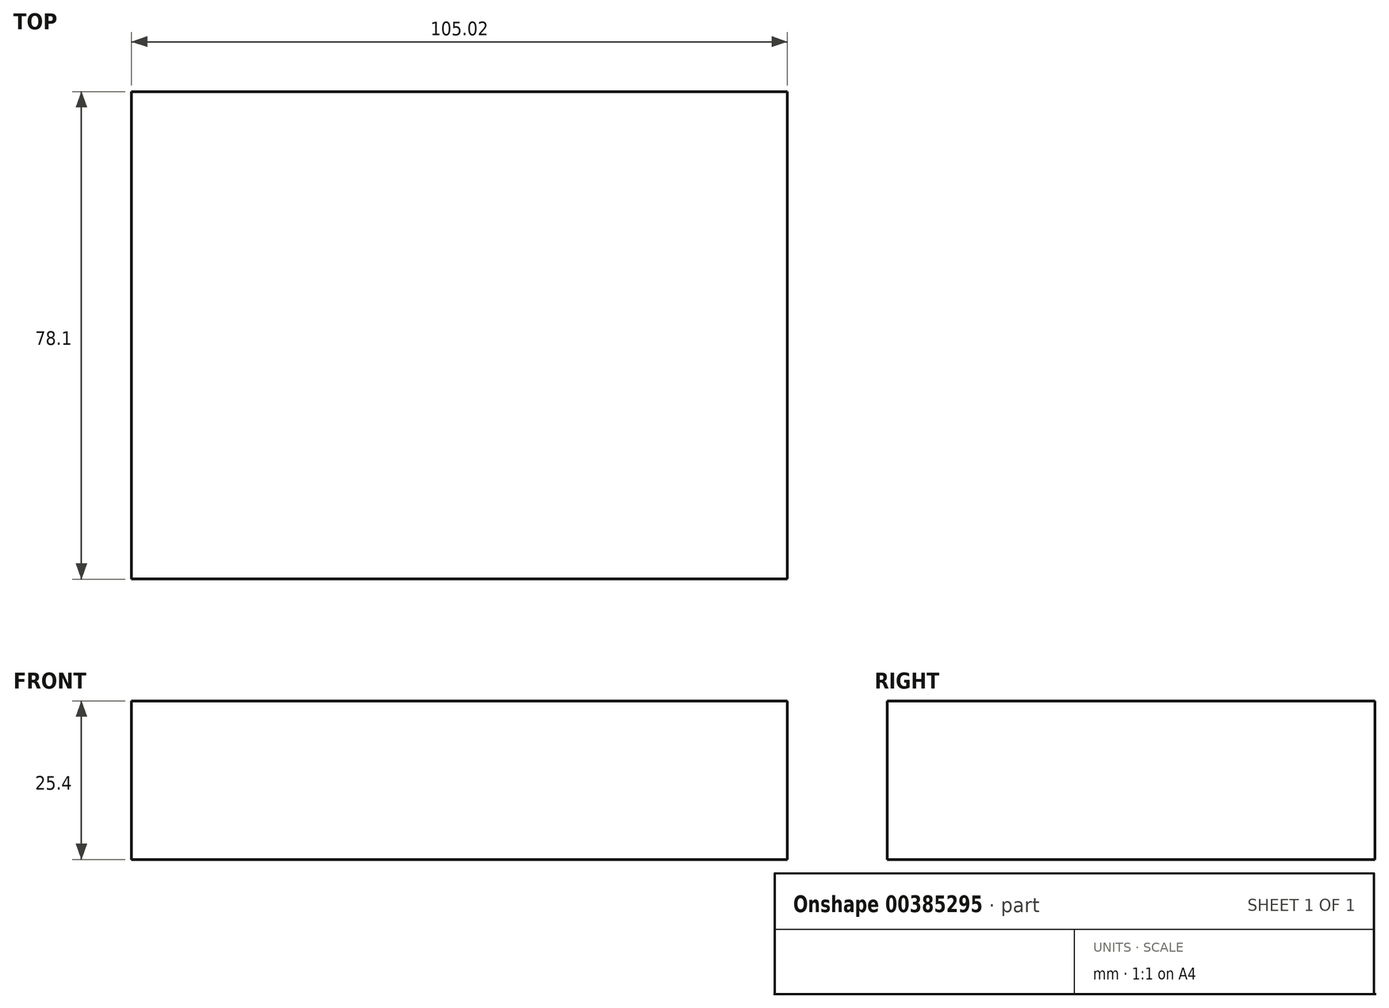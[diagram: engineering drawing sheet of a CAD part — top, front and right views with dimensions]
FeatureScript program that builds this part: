
annotation { "Feature Type Name" : "Feature", "Feature Type Description" : "" }
export const myFeature = defineFeature(function(context is Context, id is Id, definition is map)
    precondition{}
    {
        {
            var Q0;
            Q0=qCreatedBy(makeId("Top.planeOp"),FACE);
            var sketch = newSketch(context, id + "F0", { "sketchPlane" : qUnion([Q0])});
            skLineSegment(sketch, "E0.bottom", {"start": v(52.5, -39.05) * mm, "end": v(-52.5, -39.05) * mm});
            skLineSegment(sketch, "E0.top", {"start": v(52.5, 39.05) * mm, "end": v(-52.5, 39.05) * mm});
            skLineSegment(sketch, "E0.left", {"start": v(52.5, -39.05) * mm, "end": v(52.5, 39.05) * mm});
            skLineSegment(sketch, "E0.right", {"start": v(-52.5, -39.05) * mm, "end": v(-52.5, 39.05) * mm});
            skPoint(sketch, "E0.middle", {"position": v(0, 0) * mm});
            skSolve(sketch);
        }
        {
            var Q0;
            Q0 = qSketchRegion(id + "F0", true);
            extrude(context, id + "F1", {"entities" : qUnion([Q0]), "depth" : 25.4 * mm});
        }
    });
